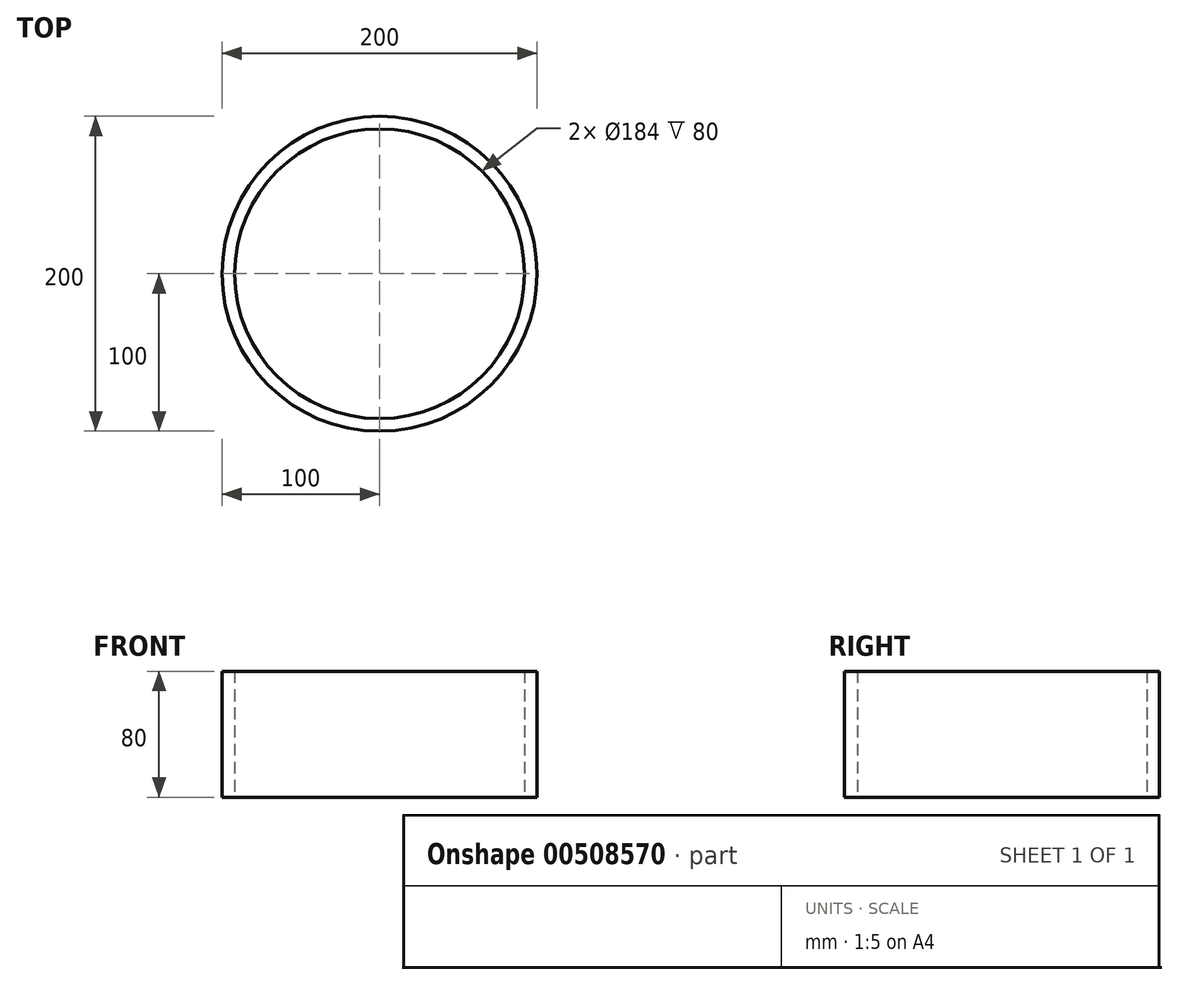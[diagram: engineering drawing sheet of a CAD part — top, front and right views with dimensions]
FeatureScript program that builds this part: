
annotation { "Feature Type Name" : "Feature", "Feature Type Description" : "" }
export const myFeature = defineFeature(function(context is Context, id is Id, definition is map)
    precondition{}
    {
        {
            var Q0;
            Q0=qCreatedBy(makeId("Top.planeOp"),FACE);
            var sketch = newSketch(context, id + "F0", { "sketchPlane" : qUnion([Q0])});
            skCircle(sketch, "E0", {"center": v(0, 0) * mm, "radius": 100 * mm});
            skCircle(sketch, "E1", {"center": v(0, 0) * mm, "radius": 92 * mm});
            skSolve(sketch);
        }
        {
            var Q0;
            Q0=makeQuery(id+"F0.imprint","IMPRINT",FACE,{"disambiguationData":[TD([[makeQuery(id+"F0.imprint","IMPRINT",EDGE,{"derivedFrom":sQuery(id+"F0.wireOp",EDGE,"E0")}),1.0]])]});
            extrude(context, id + "F1", {"entities" : qUnion([Q0]), "depth" : 80 * mm});
        }
    });
